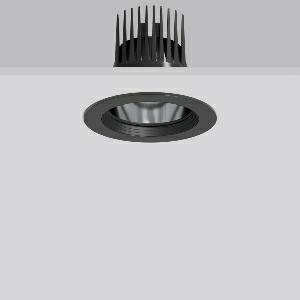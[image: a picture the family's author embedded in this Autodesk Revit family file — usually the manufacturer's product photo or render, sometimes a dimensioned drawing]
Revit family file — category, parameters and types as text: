
# Revit family: heledon_maxi_e_901778_003_76_7ea1
name_source: partatom
category: Lighting Fixtures
units: mm (PartAtom-declared; Revit-internal decimal feet)

## family parameters
Cut with Voids When Loaded = No
Host = Face
Light Source = No
Part Type = Normal
Room Calculation Point = No
Round Connector Dimension = Use Diameter
Shared = No

## types (1)
- HELEDON maxi E (1 x LED Modul 920 meat+, 2250 lm, 2000)
    Apparent Load = 33 VA
    Approval mark = CE
    CIE Flux Codes = 100 100 100 100 100
    Color Rendering = 90
    Color Temperature = 2000
    Default Elevation = 1800 mm
    Description = Series: HELEDON maxi
Round recessed downlight. Housing: die-cast aluminium, powder-coated. Black plastic ring and recessed LED to prevent glare from the side. Optical assembly with reflector made of MIRO-Silver with 98% total light reflection for outstanding efficiency - can be changed without tools. Special LED for illumination of meat included. Suitable for Recessed ceiling mounting. Installation without tools thanks to spring fastening system. Including separate LED converter with connecting cable 600 mm.High quality converter without flickering and stroboscopic effect. Through-wiring box (5 pole) available as accessory. The following accessories can be mounted without use of tools: interchangeable lenses, decorative glasses, honeycomb louvre, clear and frosted diffusers, white interchangeable plastic ring. 
Colour: deep black, matt (RAL 9005)
Diameter: 162 mm
Height: 3 mm
Cut-out diameter: 152 mm
Recess height: 200 mm
Luminaire: recess height: 135 mm
Lamp: LED
Socket: without socket
Colour temperature: meat +
System power: 33 W
Rated luminous flux: 2250 lm
Luminous efficiency: 68 lm/W
Control gear: Converter, dimmable, DALI
Protection class: II
Type of protection: IP 20
    Height = 0 mm  [stored 0 ft]
    Lamp = 1 x LED Modul 920 meat+
    Lamp Light Flux = 2250 lm
    Lamp count = 1
    Length = 162 mm
    Lifetime = 50000 h
    Luminous efficacy = 68 lm/W
    Manufacturer = RZB
    ModVariant = No
    Model = 901778.003.76
    Mounting Place = Ceiling
    Mounting Type = Recessed
    Number of Poles = 1
    OnlyDefault = Yes
    Power Factor = 1
    Product Name = HELEDON maxi E
    Product group = Recessed downlights
    ProductGroupID = 402
    Protection Class = Protection class II
    Protection Degree = IP 20
    RLX_Detail_Level = 1
    RLX_Emergency_Light_Flux = 0 lm
    RLX_Emergency_Type = 0
    RLX_Emergency_Type_DB = No
    RlxData = <blob elided: 121717 chars, md5=d88aae38>
    Socket = socket
    Standby Power = 0 W
    System Light Flux = 2250 lm
    System Power = 33 W
    Type Comments = Product without accessories
    Type Image = 901662.003.jpg
    URL = http://relux.com
    VarID = ---
    Voltage = 230 V
    Voltage Range = 220-240 V
    Weight = 0.00 kg
    Width = 0 mm  [stored 0 ft]

note: [stored X ft] marks values corroborated as IEEE doubles in the binary element streams (Revit-internal decimal feet)

## geometry (parser evidence)
native form markers: Blend x4, Sweep x12
no freeform markers — native parametric forms only
